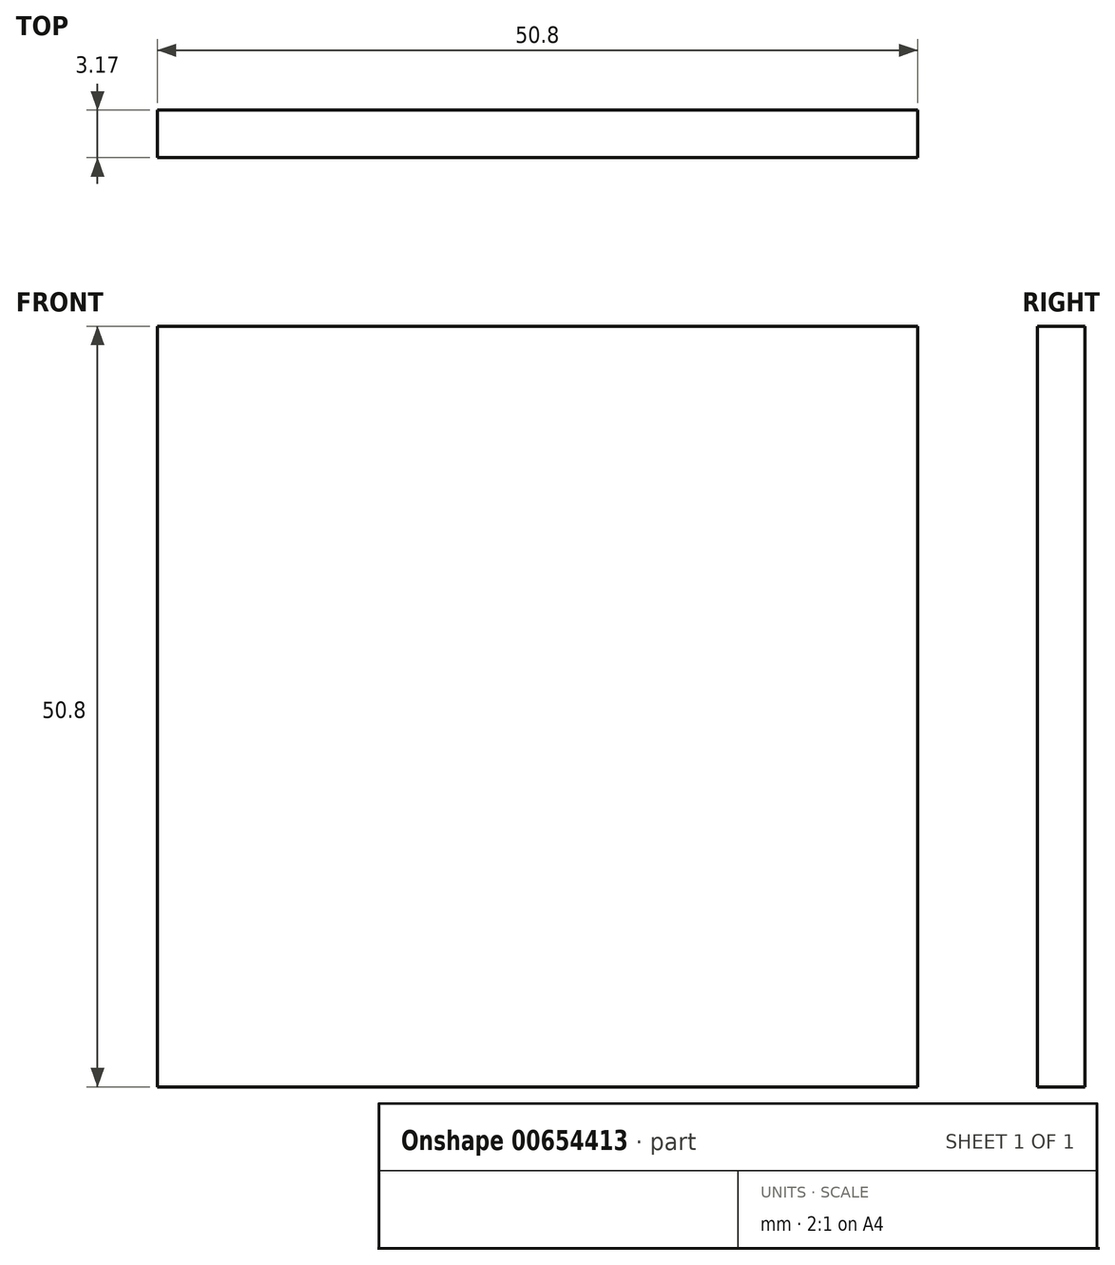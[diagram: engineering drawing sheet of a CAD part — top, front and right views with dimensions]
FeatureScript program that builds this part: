
annotation { "Feature Type Name" : "Feature", "Feature Type Description" : "" }
export const myFeature = defineFeature(function(context is Context, id is Id, definition is map)
    precondition{}
    {
        {
            var Q0;
            Q0=qCreatedBy(makeId("Front.planeOp"),FACE);
            var sketch = newSketch(context, id + "F0", { "sketchPlane" : qUnion([Q0])});
            skLineSegment(sketch, "E0.0", {"start": v(-50.8, 50.8) * mm, "end": v(-50.8, 0) * mm});
            skLineSegment(sketch, "E1.0", {"start": v(0, 50.8) * mm, "end": v(-50.8, 50.8) * mm});
            skLineSegment(sketch, "E2.0", {"start": v(0, 0) * mm, "end": v(0, 50.8) * mm});
            skLineSegment(sketch, "E3.0", {"start": v(-50.8, 0) * mm, "end": v(0, 0) * mm});
            skSolve(sketch);
        }
        {
            var Q0;
            Q0 = qSketchRegion(id + "F0", true);
            extrude(context, id + "F1", {"entities" : qUnion([Q0]), "oppositeDirection" : true, "depth" : 3.17 * mm, "offsetDistance" : 25.4 * mm});
        }
    });
